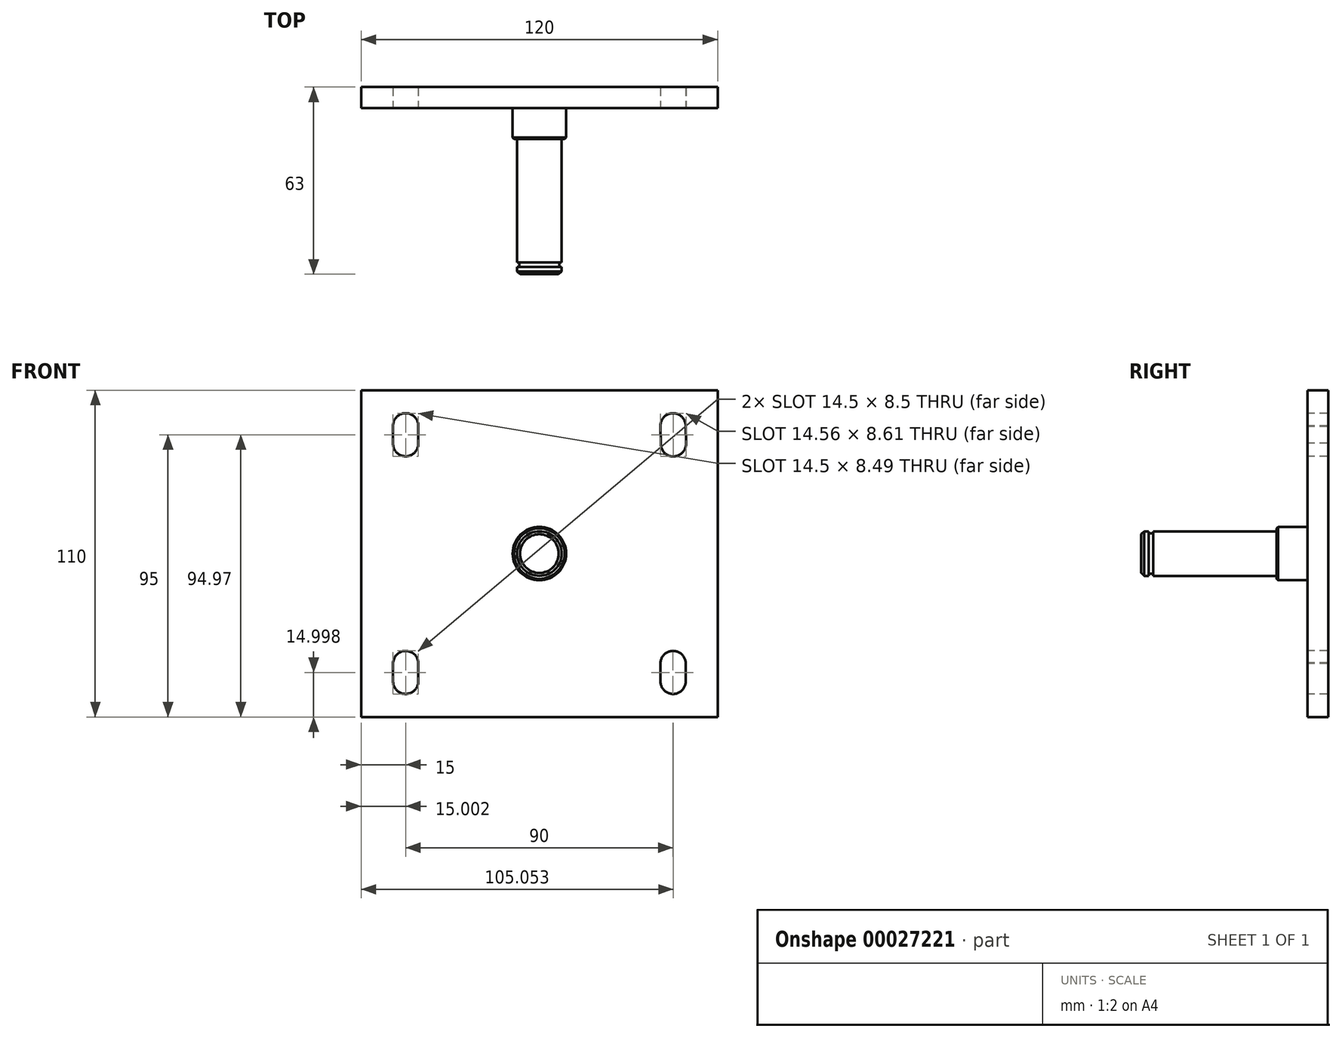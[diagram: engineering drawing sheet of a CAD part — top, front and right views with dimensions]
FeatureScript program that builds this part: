
annotation { "Feature Type Name" : "Feature", "Feature Type Description" : "" }
export const myFeature = defineFeature(function(context is Context, id is Id, definition is map)
    precondition{}
    {
        {
            var Q0;
            Q0=qCreatedBy(makeId("Front.planeOp"),FACE);
            var sketch = newSketch(context, id + "F0", { "sketchPlane" : qUnion([Q0])});
            skLineSegment(sketch, "E0.bottom", {"start": v(0, 0) * mm, "end": v(120, 0) * mm});
            skLineSegment(sketch, "E0.top", {"start": v(0, 110) * mm, "end": v(120, 110) * mm});
            skLineSegment(sketch, "E0.left", {"start": v(0, 0) * mm, "end": v(0, 110) * mm});
            skLineSegment(sketch, "E0.right", {"start": v(120, 0) * mm, "end": v(120, 110) * mm});
            skSolve(sketch);
        }
        {
            var Q0;
            Q0=makeQuery(id+"F0.imprint","IMPRINT",FACE,{"disambiguationData":[TD([[makeQuery(id+"F0.imprint","IMPRINT",EDGE,{"derivedFrom":sQuery(id+"F0.wireOp",EDGE,"E0.bottom")}),1.0]])]});
            extrude(context, id + "F1", {"entities" : qUnion([Q0]), "depth" : 7 * mm});
        }
        {
            var Q0;
            Q0=makeQuery(id+"F1.opExtrude","CAP_FACE",FACE,{"disambiguationData":[OSD([sQuery(id+"F0.wireOp",EDGE,"E0.bottom"),sQuery(id+"F0.wireOp",EDGE,"E0.top"),sQuery(id+"F0.wireOp",EDGE,"E0.left"),sQuery(id+"F0.wireOp",EDGE,"E0.right")])],"isStart":false});
            var sketch = newSketch(context, id + "F2", { "sketchPlane" : qUnion([Q0])});
            skSolve(sketch);
        }
        {
            var Q0;
            Q0=makeQuery(id+"F2.imprint","IMPRINT",FACE,{"disambiguationData":[TD([[makeQuery(id+"F2.imprint","IMPRINT",EDGE,{"derivedFrom":makeQuery(id+"F1.opExtrude","CAP_EDGE",EDGE,{"disambiguationData":[OSD([sQuery(id+"F0.wireOp",EDGE,"E0.bottom")])],"isStart":false})}),1.0]])]});
            var sketch = newSketch(context, id + "F3", { "sketchPlane" : qUnion([Q0])});
            skArc(sketch, "E1", {"start": v(10.75, 12) * mm, "mid": v(15, 7.75) * mm, "end": v(19.25, 12) * mm});
            skArc(sketch, "E2", {"start": v(19.24, 18.25) * mm, "mid": v(14.84, 22.25) * mm, "end": v(10.75, 17.93) * mm});
            skArc(sketch, "E3", {"start": v(10.75, 92.2) * mm, "mid": v(14.9, 87.75) * mm, "end": v(19.25, 92) * mm});
            skArc(sketch, "E4", {"start": v(19.25, 98) * mm, "mid": v(14.9, 102.25) * mm, "end": v(10.75, 97.8) * mm});
            skArc(sketch, "E5", {"start": v(109.25, 97.95) * mm, "mid": v(104.95, 102.25) * mm, "end": v(100.75, 97.85) * mm});
            skArc(sketch, "E6", {"start": v(100.86, 91.87) * mm, "mid": v(105.18, 87.7) * mm, "end": v(109.36, 92.02) * mm});
            skArc(sketch, "E7", {"start": v(109.25, 18) * mm, "mid": v(104.99, 22.25) * mm, "end": v(100.75, 17.98) * mm});
            skArc(sketch, "E8", {"start": v(100.75, 12.02) * mm, "mid": v(104.99, 7.75) * mm, "end": v(109.25, 12) * mm});
            skLineSegment(sketch, "E9", {"start": v(10.75, 97.8) * mm, "end": v(10.75, 92.2) * mm});
            skLineSegment(sketch, "E10", {"start": v(19.25, 98) * mm, "end": v(19.25, 92) * mm});
            skLineSegment(sketch, "E11", {"start": v(10.75, 17.93) * mm, "end": v(10.75, 12) * mm});
            skLineSegment(sketch, "E12", {"start": v(19.24, 18.25) * mm, "end": v(19.25, 12) * mm});
            skLineSegment(sketch, "E13", {"start": v(109.25, 18) * mm, "end": v(109.25, 12) * mm});
            skLineSegment(sketch, "E14", {"start": v(100.75, 98) * mm, "end": v(100.86, 91.87) * mm});
            skLineSegment(sketch, "E15", {"start": v(109.25, 97.95) * mm, "end": v(109.36, 92.02) * mm});
            skLineSegment(sketch, "E16", {"start": v(100.75, 17.98) * mm, "end": v(100.75, 12.02) * mm});
            skCircle(sketch, "E17", {"center": v(60, 54.8) * mm, "radius": 9.05 * mm});
            skPoint(sketch, "E18.start.orphan", {"position": v(0, 109.8) * mm});
            skSolve(sketch);
        }
        {
            var Q0;
            {var subQ2=sQuery(id+"F3.wireOp",EDGE,"E1");Q0=makeQuery(id+"F3.imprint","IMPRINT",FACE,{"disambiguationData":[TD([[makeQuery(id+"F3.imprint","IMPRINT",EDGE,{"derivedFrom":subQ2}),1.0]])]});}
            var Q1;
            Q1=makeQuery(id+"F3.imprint","IMPRINT",FACE,{"disambiguationData":[TD([[makeQuery(id+"F3.imprint","IMPRINT",EDGE,{"derivedFrom":sQuery(id+"F3.wireOp",EDGE,"E3")}),1.0]])]});
            var Q2;
            {var subQ2=sQuery(id+"F3.wireOp",EDGE,"E6");Q2=makeQuery(id+"F3.imprint","IMPRINT",FACE,{"disambiguationData":[TD([[makeQuery(id+"F3.imprint","IMPRINT",EDGE,{"derivedFrom":subQ2}),1.0]])]});}
            var Q3;
            Q3=makeQuery(id+"F3.imprint","IMPRINT",FACE,{"disambiguationData":[TD([[makeQuery(id+"F3.imprint","IMPRINT",EDGE,{"derivedFrom":sQuery(id+"F3.wireOp",EDGE,"E7")}),1.0]])]});
            extrude(context, id + "F4", {"entities" : qUnion([Q0, Q1, Q2, Q3]), "operationType" : NewBodyOperationType.REMOVE, "oppositeDirection" : true, "depth" : 25 * mm});
        }
        {
            var Q0;
            Q0=makeQuery(id+"F2.imprint","IMPRINT",FACE,{"disambiguationData":[TD([[makeQuery(id+"F2.imprint","IMPRINT",EDGE,{"derivedFrom":makeQuery(id+"F1.opExtrude","CAP_EDGE",EDGE,{"disambiguationData":[OSD([sQuery(id+"F0.wireOp",EDGE,"E0.bottom")])],"isStart":false})}),1.0]])]});
            var sketch = newSketch(context, id + "F5", { "sketchPlane" : qUnion([Q0])});
            skCircle(sketch, "E19", {"center": v(60, 55) * mm, "radius": 9 * mm});
            skSolve(sketch);
        }
        {
            var Q0;
            Q0=makeQuery(id+"F5.imprint","IMPRINT",FACE,{"disambiguationData":[TD([[makeQuery(id+"F5.imprint","IMPRINT",EDGE,{"derivedFrom":sQuery(id+"F5.wireOp",EDGE,"E19")}),1.0]])]});
            extrude(context, id + "F6", {"entities" : qUnion([Q0]), "operationType" : NewBodyOperationType.ADD, "depth" : 10.5 * mm});
        }
        {
            var Q0;
            Q0=makeQuery(id+"F6.opExtrude","CAP_FACE",FACE,{"disambiguationData":[OSD([sQuery(id+"F5.wireOp",EDGE,"E19")])],"isStart":false});
            var sketch = newSketch(context, id + "F7", { "sketchPlane" : qUnion([Q0])});
            skCircle(sketch, "E20", {"center": v(60, 55) * mm, "radius": 7.5 * mm});
            skSolve(sketch);
        }
        {
            var Q0;
            Q0=makeQuery(id+"F7.imprint","IMPRINT",FACE,{"disambiguationData":[TD([[makeQuery(id+"F7.imprint","IMPRINT",EDGE,{"derivedFrom":sQuery(id+"F7.wireOp",EDGE,"E20")}),1.0]])]});
            extrude(context, id + "F8", {"entities" : qUnion([Q0]), "operationType" : NewBodyOperationType.ADD, "depth" : 41.5 * mm});
        }
        {
            var Q0;
            Q0=makeQuery(id+"F8.opExtrude","CAP_FACE",FACE,{"disambiguationData":[OSD([sQuery(id+"F7.wireOp",EDGE,"E20")])],"isStart":false});
            var sketch = newSketch(context, id + "F9", { "sketchPlane" : qUnion([Q0])});
            skCircle(sketch, "E21", {"center": v(60, 55) * mm, "radius": 6.75 * mm});
            skSolve(sketch);
        }
        {
            var Q0;
            Q0=makeQuery(id+"F9.imprint","IMPRINT",FACE,{"disambiguationData":[TD([[makeQuery(id+"F9.imprint","IMPRINT",EDGE,{"derivedFrom":sQuery(id+"F9.wireOp",EDGE,"E21")}),1.0]])]});
            extrude(context, id + "F10", {"entities" : qUnion([Q0]), "operationType" : NewBodyOperationType.ADD, "depth" : 1.5 * mm});
        }
        {
            var Q0;
            Q0=makeQuery(id+"F10.opExtrude","CAP_FACE",FACE,{"disambiguationData":[OSD([sQuery(id+"F9.wireOp",EDGE,"E21")])],"isStart":false});
            var sketch = newSketch(context, id + "F11", { "sketchPlane" : qUnion([Q0])});
            skCircle(sketch, "E22", {"center": v(60, 55) * mm, "radius": 7.5 * mm});
            skSolve(sketch);
        }
        {
            var Q0;
            Q0=makeQuery(id+"F11.imprint","IMPRINT",FACE,{"disambiguationData":[TD([[makeQuery(id+"F11.imprint","IMPRINT",EDGE,{"derivedFrom":sQuery(id+"F11.wireOp",EDGE,"E22")}),1.0]])]});
            var Q1;
            Q1=makeQuery(id+"F11.imprint","IMPRINT",FACE,{"disambiguationData":[TD([[makeQuery(id+"F11.imprint","IMPRINT",EDGE,{"derivedFrom":makeQuery(id+"F10.opExtrude","CAP_EDGE",EDGE,{"disambiguationData":[OSD([sQuery(id+"F9.wireOp",EDGE,"E21")])],"isStart":false})}),1.0]])]});
            extrude(context, id + "F12", {"entities" : qUnion([Q0, Q1]), "operationType" : NewBodyOperationType.ADD, "depth" : 2.5 * mm});
        }
        {
            var Q0;
            Q0=makeQuery(id+"F12.opExtrude","CAP_EDGE",EDGE,{"disambiguationData":[OSD([sQuery(id+"F11.wireOp",EDGE,"E22")])],"isStart":false});
            chamfer(context, id + "F13", {"entities" : qUnion([Q0]), "width" : 1 * mm, "tangentPropagation" : true});
        }
        {
            var Q0;
            Q0=makeQuery(id+"F6.opExtrude","CAP_EDGE",EDGE,{"disambiguationData":[OSD([sQuery(id+"F5.wireOp",EDGE,"E19")])],"isStart":false});
            chamfer(context, id + "F14", {"entities" : qUnion([Q0]), "width" : 0.5 * mm, "tangentPropagation" : true});
        }
    });
